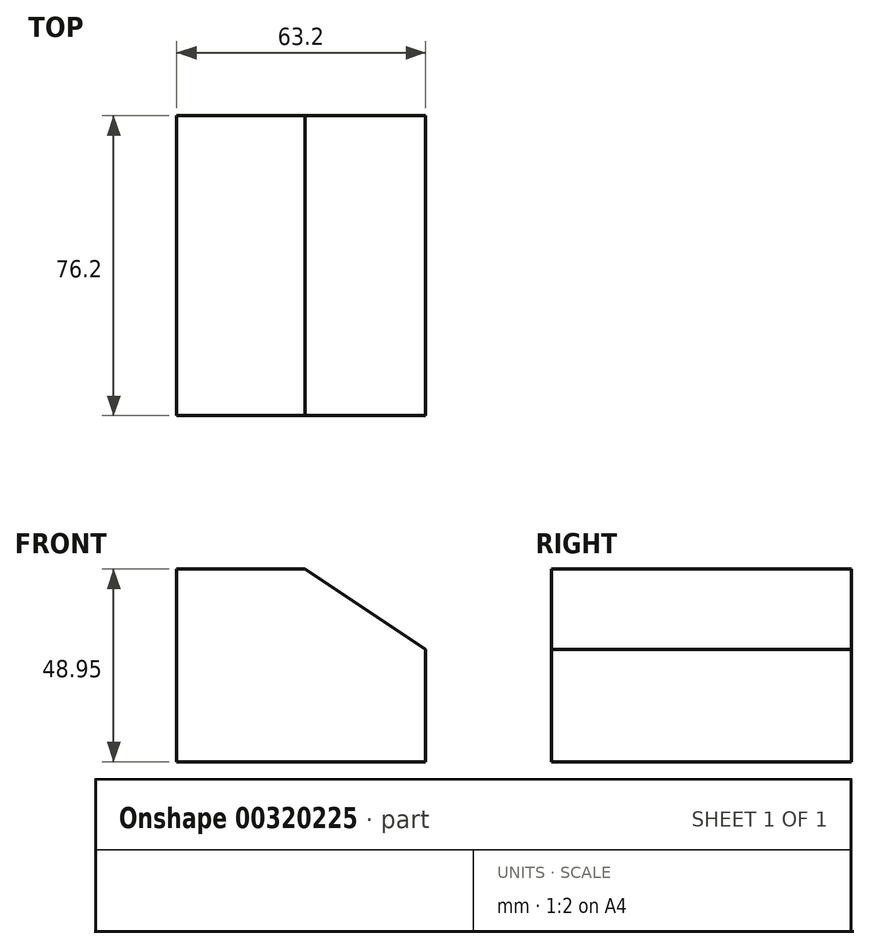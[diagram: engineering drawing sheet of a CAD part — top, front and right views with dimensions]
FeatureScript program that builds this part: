
annotation { "Feature Type Name" : "Feature", "Feature Type Description" : "" }
export const myFeature = defineFeature(function(context is Context, id is Id, definition is map)
    precondition{}
    {
        {
            var Q0;
            Q0=qCreatedBy(makeId("Front.planeOp"),FACE);
            var sketch = newSketch(context, id + "F0", { "sketchPlane" : qUnion([Q0])});
            skLineSegment(sketch, "E0", {"start": v(-50.3, -45.6) * mm, "end": v(-50.3, -94.55) * mm});
            skLineSegment(sketch, "E1", {"start": v(-50.3, -94.55) * mm, "end": v(12.9, -94.55) * mm});
            skLineSegment(sketch, "E2", {"start": v(12.9, -94.55) * mm, "end": v(12.9, -66.03) * mm});
            skLineSegment(sketch, "E3", {"start": v(12.9, -66.03) * mm, "end": v(-17.74, -45.6) * mm});
            skLineSegment(sketch, "E4", {"start": v(-17.74, -45.6) * mm, "end": v(-50.3, -45.6) * mm});
            skSolve(sketch);
        }
        {
            var Q0;
            Q0=makeQuery(id+"F0.imprint","IMPRINT",FACE,{"disambiguationData":[TD([[makeQuery(id+"F0.imprint","IMPRINT",EDGE,{"derivedFrom":sQuery(id+"F0.wireOp",EDGE,"E0")}),1.0]])]});
            extrude(context, id + "F1", {"entities" : qUnion([Q0]), "oppositeDirection" : true, "depth" : 76.2 * mm});
        }
    });
